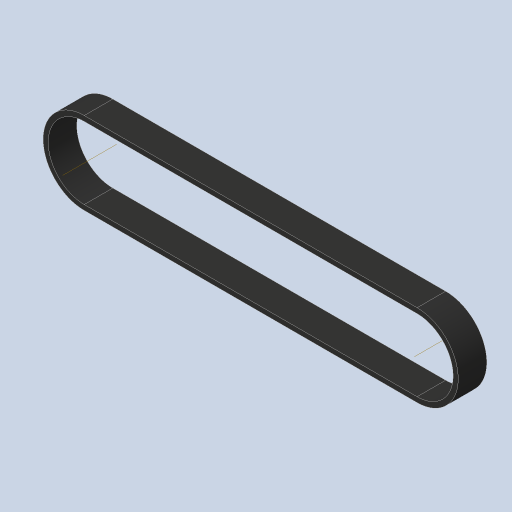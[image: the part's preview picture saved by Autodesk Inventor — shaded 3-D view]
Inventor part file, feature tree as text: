
AUTODESK INVENTOR PART (.ipt)
format: ipt  version: 2023.4 (Build 274418000, 418)  size: 166,400 bytes
history: native  units: in
note: dims shown in document units (in); Inventor stores cm internally (conversion verified against a paired STEP export)
features: sketch x3, extrude x1, other x1, projected_geometry x1
ambient origin geometry x8: Origin, YZ Plane, XZ Plane, XY Plane, X Axis, Y Axis, Z Axis, Center Point
bodies: Body1 (feature_tree)
feature tree (6):
  sketch  "Sketch2"  dims[d0=0.9023in d1=0.9023in]
  extrude  "Extrusion2"  Depth=0.9023in
  sketch  "Sketch5"  dims[d3=1.4174in d5=3.8976in d9=0.0787in d10=0.0598in d11=0.0299in d12=0.0219in d13=0.0219in d14=0.0059in d15=0.0059in d20=0.3346in d21=0.0in d22=0.0787in d23=0.0598in d24=0.0299in d25=0.0219in d26=0.0219in d27=0.0059in d28=0.0059in d29=0.0299in d30=0.0394in d31=0.0787in d32=0.0232in d34=0.0219in d35=0.0in d36=0.0in d37=0.0059in d38=0.0022in d39=0.0022in d40=0.0in d41=0.0in d42=0.0081in d43=0.0081in d44=0.0299in]
  other  "Work Axis1"
  sketch  "Sketch4"  dims[d2=1.4174in]
  projected_geometry  "Projected Loop1"
